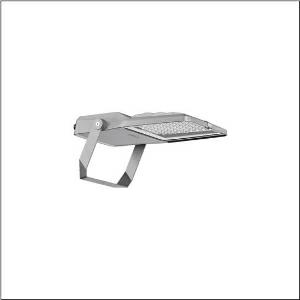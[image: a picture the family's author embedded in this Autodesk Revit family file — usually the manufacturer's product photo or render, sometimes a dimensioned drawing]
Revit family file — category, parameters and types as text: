
# Revit family: floodlight_fl_21_iq_mini___pl33t_5xa7772b1f1a_dd0a
name_source: partatom
category: Lighting Fixtures
units: mm (PartAtom-declared; Revit-internal decimal feet)

## family parameters
Cut with Voids When Loaded = No
Host = Face
Light Source = No
Part Type = Normal
Room Calculation Point = No
Round Connector Dimension = Use Diameter
Shared = No

## types (1)
- --- (1 x LED, 5110 lm, 45.5 W, 2200K)
    Apparent Load = 46 VA
    CIE Flux Codes = 26 75 99 100 100
    Color Rendering = 70
    Color Temperature = 2200K
    Default Elevation = 1800 mm
    Description = Floodlight FL 21 iQ mini, floodlight, primary light control with lens, of PMMA, primary optical cover: protective disc, of toughened safety glass, transparent, light distribution: PL33T, light emission: direct distribution, installation type: surface-mounted, lamps: LED, High Power LED, rated values: 5.110lm | 45,5W | 112,3lm/W (begin service life); end service life: 5.110lm | 48W; at 50% lumin. flux: 2.555lm | 21,4W | 119,4lm/W, colour temperature: 2200K, colour rendering: CRI > 70, light colour: 722, light setting 1 begin service life: 100% | 5.110lm | 45,5W | 112,3lm/W | 2.200K, light setting 1 end service life: 48W, further light settings possible, control: Street-Remote, Auto-Match, Temp-Guard, Night-Set, Smart-Wire, Desk-Remote (wireless, voltage-free reading and setting of iQ features in the workshop via application-optimized NFC function/RFID function), optimised constant luminous flux control (CLO 2.0), pre-setting: linear dimming characteristic, with terminal, 6-pole, mains connection: 220..240V, AC, 50/60Hz, luminaire housing, of diecast aluminium, powder-coated, SITECO metallic grey (DB 702S), corrosivity category C5 mid according to DIN EN ISO 12944suitable for swimming poolschlorine-resistant, sealing non-destructively replaceable, mounting bracket, of steel, galvanised, powder-coated, SITECO metallic grey (DB 702S), protection rating (complete): IP66, insulation class (complete): insulation class II (safety insulation), certification: CE, ENEC, VDE, protection symbol: D, impact resistance: IK08, permissible operating ambient temperature: -40..+40°C, permissible operating ambient temperature for outdoor applications: -40..+50°C, standard: DIN EN 12944, LABS conformity tested according to VDMA 24364:2018-05, packaging unit: 1 piece

Light Distribution: PL33T
    Height = 70 mm
    Lamp = 1 x LED
    Lamp Light Flux = 5110 lm
    Lamp Power = 45.5 W
    Lamp count = 1
    Length = 485 mm
    Luminous efficacy = 112 lm/W
    Manufacturer = Siteco
    ModVariant = No
    Model = 5XA7772B1F1A
    Number of Poles = 1
    OnlyDefault = Yes
    Power Factor = 1
    Product Name = Floodlight FL 21 iQ mini | PL33T
    Product group = floodlight | pylon annexe
    ProductGroupID = 6201
    Protection Class = Protection class II
    Protection Degree = IP 66
    RLX_Detail_Level = 1
    RLX_Emergency_Light_Flux = 0 lm
    RLX_Emergency_Type = 0
    RLX_Emergency_Type_DB = No
    RlxData = <blob elided: 96261 chars, md5=7c6ddd4c>
    Socket = socket
    Standby Power = 0 W
    System Light Flux = 5110 lm
    System Power = 46 W
    Type Comments = factory setting: luminous flux: 100 % | dim-lin: 254 | 463 mA
    Type Image = l_1006845.jpg
    URL = http://relux.com
    VarID = @adj_149635
    Voltage = 0 V
    Weight = 0.00 kg
    Width = 337 mm

## geometry (parser evidence)
native form markers: Blend x4, Sweep x14
no freeform markers — native parametric forms only
